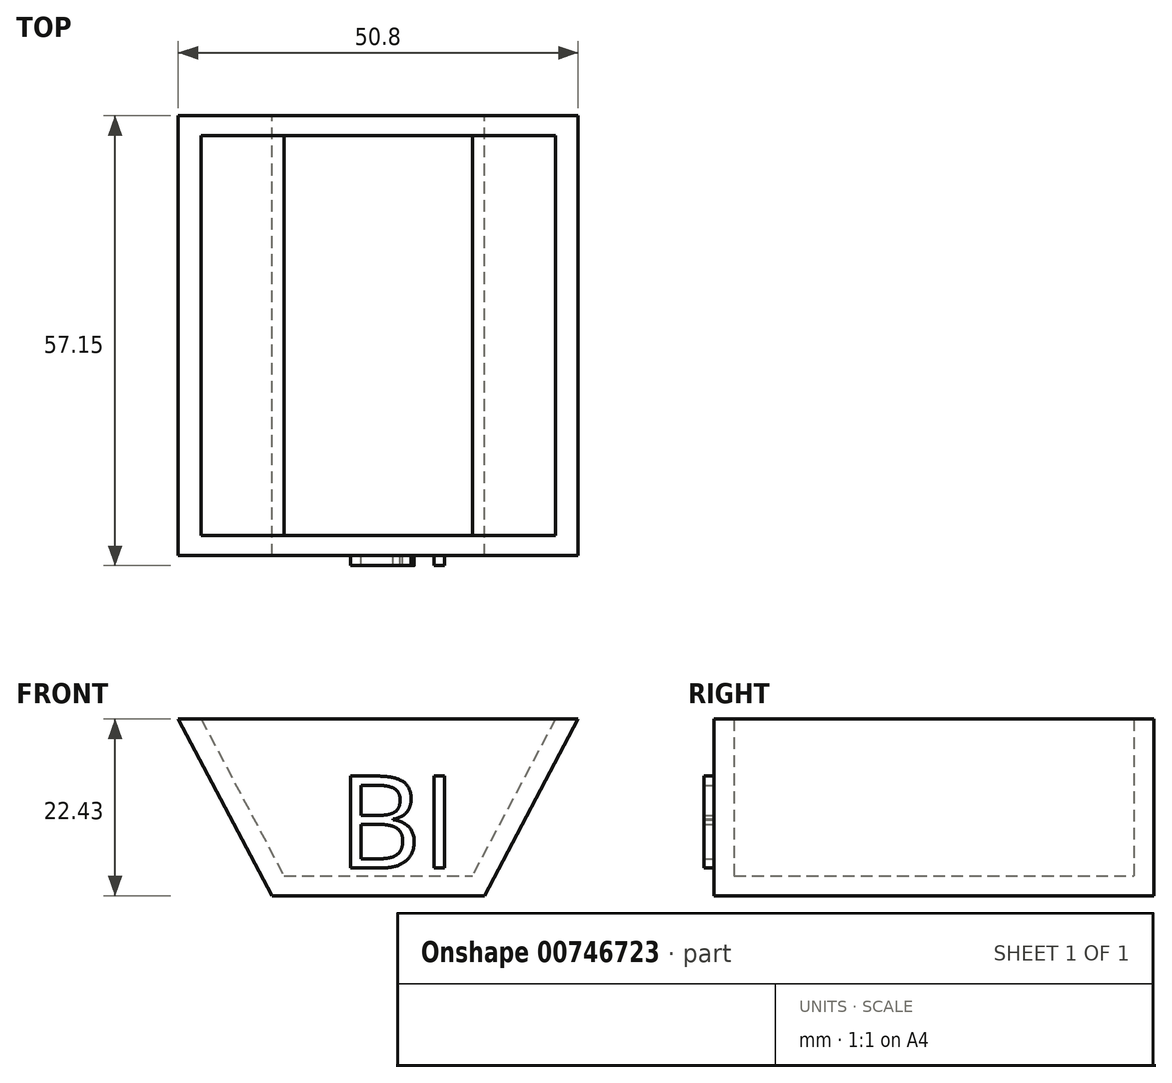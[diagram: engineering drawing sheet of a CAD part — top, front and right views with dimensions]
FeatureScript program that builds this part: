
annotation { "Feature Type Name" : "Feature", "Feature Type Description" : "" }
export const myFeature = defineFeature(function(context is Context, id is Id, definition is map)
    precondition{}
    {
        {
            var Q0;
            Q0=qCreatedBy(makeId("Front.planeOp"),FACE);
            var sketch = newSketch(context, id + "F0", { "sketchPlane" : qUnion([Q0])});
            skLineSegment(sketch, "E0", {"start": v(-34.89, 18.9) * mm, "end": v(15.91, 18.9) * mm});
            skPoint(sketch, "E1.startSnap0", {"position": v(-9.49, 18.9) * mm});
            skLineSegment(sketch, "E2", {"start": v(-34.89, 18.9) * mm, "end": v(-22.98, -3.54) * mm});
            skLineSegment(sketch, "E3", {"start": v(15.91, 18.9) * mm, "end": v(4, -3.54) * mm});
            skLineSegment(sketch, "E4", {"start": v(-22.98, -3.54) * mm, "end": v(4, -3.54) * mm});
            skSolve(sketch);
        }
        {
            var Q0;
            Q0=makeQuery(id+"F0.imprint","IMPRINT",FACE,{"disambiguationData":[TD([[makeQuery(id+"F0.imprint","IMPRINT",EDGE,{"derivedFrom":sQuery(id+"F0.wireOp",EDGE,"E0")}),-1.0]])]});
            extrude(context, id + "F1", {"entities" : qUnion([Q0]), "depth" : 55.88 * mm, "offsetDistance" : 25.4 * mm});
        }
        {
            var Q0;
            Q0=makeQuery(id+"F1.opExtrude","SWEPT_FACE",FACE,{"disambiguationData":[OSD([sQuery(id+"F0.wireOp",EDGE,"E0")])]});
            shell(context, id + "F2", {"entities" : qUnion([Q0]), "thickness" : 2.54 * mm});
        }
        {
            var Q0;
            Q0=makeQuery(id+"F1.opExtrude","CAP_FACE",FACE,{"disambiguationData":[OSD([sQuery(id+"F0.wireOp",EDGE,"E0"),sQuery(id+"F0.wireOp",EDGE,"E2"),sQuery(id+"F0.wireOp",EDGE,"E3"),sQuery(id+"F0.wireOp",EDGE,"E4")])],"isStart":false});
            var sketch = newSketch(context, id + "F3", { "sketchPlane" : qUnion([Q0])});
            skText(sketch, "E5", { "text": "BI", "fontName": "OpenSans-Regular.ttf"});
            const initialGuessF3  = {"E5": [-0.0146, 0, 1, 0, 0.01176]};
            skSetInitialGuess(sketch, initialGuessF3);
            skSolve(sketch);
        }
        {
            var Q0;
            Q0 = qSketchRegion(id + "F3", true);
            extrude(context, id + "F4", {"entities" : qUnion([Q0]), "operationType" : NewBodyOperationType.ADD, "depth" : 1.27 * mm, "offsetDistance" : 25.4 * mm});
        }
    });
